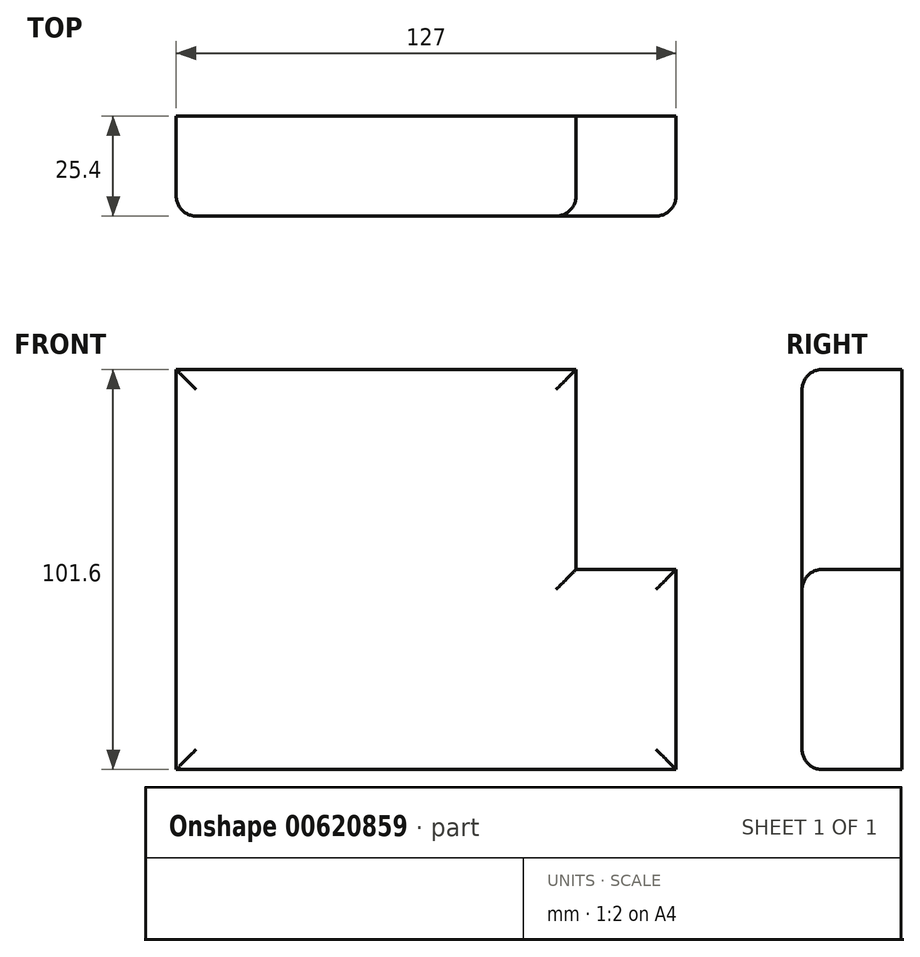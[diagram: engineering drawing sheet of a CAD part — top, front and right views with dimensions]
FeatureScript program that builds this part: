
annotation { "Feature Type Name" : "Feature", "Feature Type Description" : "" }
export const myFeature = defineFeature(function(context is Context, id is Id, definition is map)
    precondition{}
    {
        {
            var Q0;
            Q0=qCreatedBy(makeId("Front.planeOp"),FACE);
            var sketch = newSketch(context, id + "F0", { "sketchPlane" : qUnion([Q0])});
            skLineSegment(sketch, "E0", {"start": v(-101.6, 101.6) * mm, "end": v(-101.6, 0) * mm});
            skLineSegment(sketch, "E1", {"start": v(-101.6, 0) * mm, "end": v(25.4, 0) * mm});
            skLineSegment(sketch, "E2", {"start": v(25.4, 0) * mm, "end": v(25.4, 50.8) * mm});
            skLineSegment(sketch, "E3", {"start": v(25.4, 50.8) * mm, "end": v(0, 50.8) * mm});
            skLineSegment(sketch, "E4", {"start": v(0, 50.8) * mm, "end": v(0, 101.6) * mm});
            skLineSegment(sketch, "E5", {"start": v(0, 101.6) * mm, "end": v(-101.6, 101.6) * mm});
            skSolve(sketch);
        }
        {
            var Q0;
            Q0=makeQuery(id+"F0.imprint","IMPRINT",FACE,{"disambiguationData":[TD([[makeQuery(id+"F0.imprint","IMPRINT",EDGE,{"derivedFrom":sQuery(id+"F0.wireOp",EDGE,"E0")}),1.0]])]});
            extrude(context, id + "F1", {"entities" : qUnion([Q0]), "depth" : 25.4 * mm, "offsetDistance" : 25.4 * mm});
        }
        {
            var Q0;
            Q0=makeQuery(id+"F1.opExtrude","CAP_FACE",FACE,{"disambiguationData":[OSD([sQuery(id+"F0.wireOp",EDGE,"E0"),sQuery(id+"F0.wireOp",EDGE,"E1"),sQuery(id+"F0.wireOp",EDGE,"E2"),sQuery(id+"F0.wireOp",EDGE,"E3"),sQuery(id+"F0.wireOp",EDGE,"E4"),sQuery(id+"F0.wireOp",EDGE,"E5")])],"isStart":false});
            fillet(context, id + "F2", {"entities" : qUnion([Q0]), "radius" : 5.08 * mm, "tangentPropagation" : true, "allowEdgeOverflow" : false});
        }
    });
